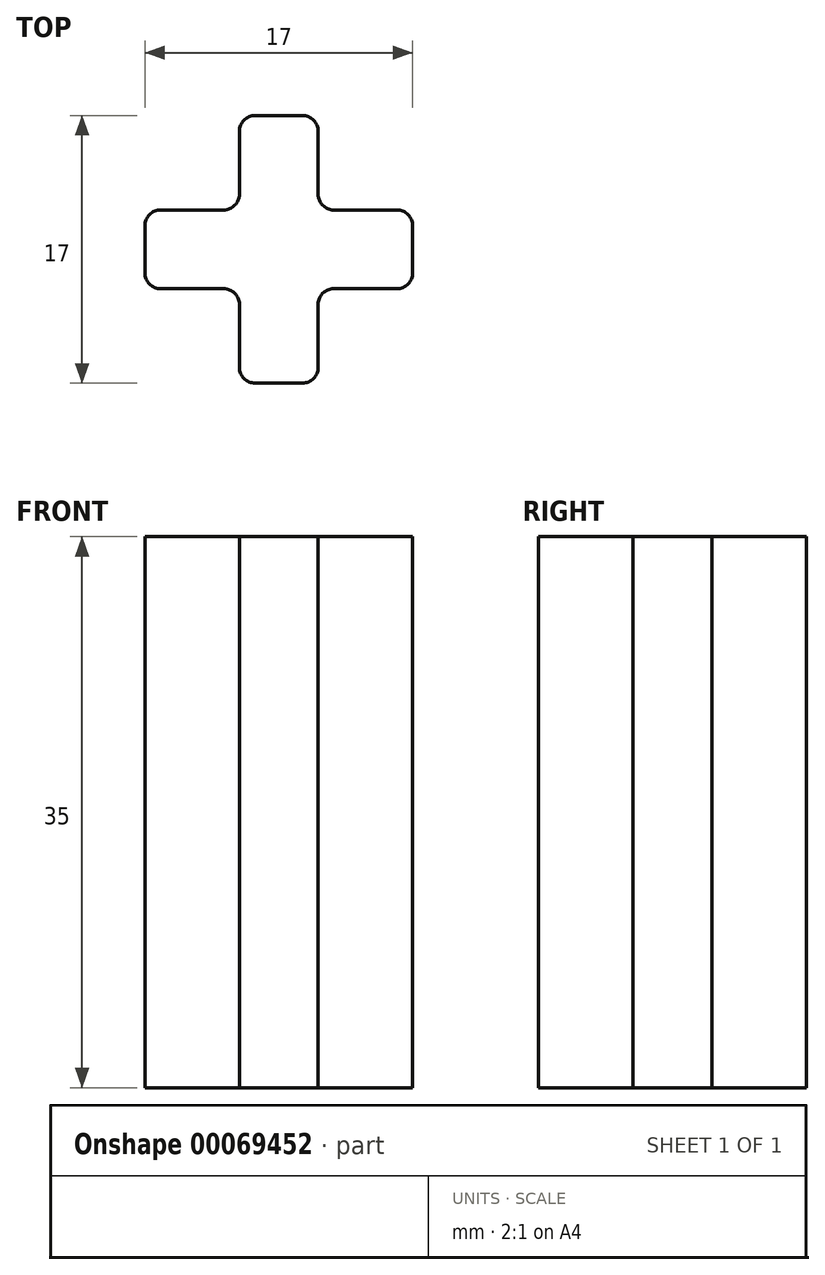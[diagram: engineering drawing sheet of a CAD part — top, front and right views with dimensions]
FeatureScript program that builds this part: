
annotation { "Feature Type Name" : "Feature", "Feature Type Description" : "" }
export const myFeature = defineFeature(function(context is Context, id is Id, definition is map)
    precondition{}
    {
        {
            var Q0;
            Q0=qCreatedBy(makeId("Top.planeOp"),FACE);
            var sketch = newSketch(context, id + "F0", { "sketchPlane" : qUnion([Q0])});
            skLineSegment(sketch, "E0", {"start": v(-2.5, -2.5) * mm, "end": v(-2.5, -8.5) * mm});
            skLineSegment(sketch, "E1", {"start": v(-2.5, -8.5) * mm, "end": v(2.5, -8.5) * mm});
            skLineSegment(sketch, "E2", {"start": v(2.5, -8.5) * mm, "end": v(2.5, -2.5) * mm});
            skLineSegment(sketch, "E3", {"start": v(2.5, -2.5) * mm, "end": v(8.5, -2.5) * mm});
            skLineSegment(sketch, "E4", {"start": v(8.5, -2.5) * mm, "end": v(8.5, 2.5) * mm});
            skLineSegment(sketch, "E5", {"start": v(8.5, 2.5) * mm, "end": v(2.5, 2.5) * mm});
            skLineSegment(sketch, "E6", {"start": v(2.5, 2.5) * mm, "end": v(2.5, 8.5) * mm});
            skLineSegment(sketch, "E7", {"start": v(2.5, 8.5) * mm, "end": v(-2.5, 8.5) * mm});
            skLineSegment(sketch, "E8", {"start": v(-2.5, 8.5) * mm, "end": v(-2.5, 2.5) * mm});
            skLineSegment(sketch, "E9", {"start": v(-2.5, 2.5) * mm, "end": v(-8.5, 2.5) * mm});
            skLineSegment(sketch, "E10", {"start": v(-8.5, 2.5) * mm, "end": v(-8.5, -2.5) * mm});
            skLineSegment(sketch, "E11", {"start": v(-8.5, -2.5) * mm, "end": v(-2.5, -2.5) * mm});
            skSolve(sketch);
        }
        {
            var Q0;
            Q0 = qSketchRegion(id + "F0", true);
            extrude(context, id + "F1", {"entities" : qUnion([Q0]), "depth" : 35 * mm});
        }
        {
            var Q0;
            Q0=makeQuery(id+"F1.opExtrude","SWEPT_EDGE",EDGE,{"disambiguationData":[OSD([sQuery(id+"F0.wireOp",EDGE,"E2"),sQuery(id+"F0.wireOp",EDGE,"E3")])]});
            var Q1;
            Q1=makeQuery(id+"F1.opExtrude","SWEPT_EDGE",EDGE,{"disambiguationData":[OSD([sQuery(id+"F0.wireOp",EDGE,"E0"),sQuery(id+"F0.wireOp",EDGE,"E11")])]});
            fillet(context, id + "F2", {"entities" : qUnion([Q0, Q1]), "radius" : 1 * mm, "tangentPropagation" : true, "allowEdgeOverflow" : false});
        }
        {
            var Q0;
            Q0=makeQuery(id+"F1.opExtrude","SWEPT_EDGE",EDGE,{"disambiguationData":[OSD([sQuery(id+"F0.wireOp",EDGE,"E8"),sQuery(id+"F0.wireOp",EDGE,"E9")])]});
            var Q1;
            Q1=makeQuery(id+"F1.opExtrude","SWEPT_EDGE",EDGE,{"disambiguationData":[OSD([sQuery(id+"F0.wireOp",EDGE,"E5"),sQuery(id+"F0.wireOp",EDGE,"E6")])]});
            fillet(context, id + "F3", {"entities" : qUnion([Q0, Q1]), "radius" : 1 * mm, "allowEdgeOverflow" : false});
        }
        {
            var Q0;
            Q0=makeQuery(id+"F1.opExtrude","SWEPT_EDGE",EDGE,{"disambiguationData":[OSD([sQuery(id+"F0.wireOp",EDGE,"E0"),sQuery(id+"F0.wireOp",EDGE,"E1")])]});
            var Q1;
            Q1=makeQuery(id+"F1.opExtrude","SWEPT_EDGE",EDGE,{"disambiguationData":[OSD([sQuery(id+"F0.wireOp",EDGE,"E1"),sQuery(id+"F0.wireOp",EDGE,"E2")])]});
            var Q2;
            Q2=makeQuery(id+"F1.opExtrude","SWEPT_EDGE",EDGE,{"disambiguationData":[OSD([sQuery(id+"F0.wireOp",EDGE,"E10"),sQuery(id+"F0.wireOp",EDGE,"E11")])]});
            var Q3;
            Q3=makeQuery(id+"F1.opExtrude","SWEPT_EDGE",EDGE,{"disambiguationData":[OSD([sQuery(id+"F0.wireOp",EDGE,"E9"),sQuery(id+"F0.wireOp",EDGE,"E10")])]});
            var Q4;
            Q4=makeQuery(id+"F1.opExtrude","SWEPT_EDGE",EDGE,{"disambiguationData":[OSD([sQuery(id+"F0.wireOp",EDGE,"E7"),sQuery(id+"F0.wireOp",EDGE,"E8")])]});
            var Q5;
            Q5=makeQuery(id+"F1.opExtrude","SWEPT_EDGE",EDGE,{"disambiguationData":[OSD([sQuery(id+"F0.wireOp",EDGE,"E6"),sQuery(id+"F0.wireOp",EDGE,"E7")])]});
            var Q6;
            Q6=makeQuery(id+"F1.opExtrude","SWEPT_EDGE",EDGE,{"disambiguationData":[OSD([sQuery(id+"F0.wireOp",EDGE,"E4"),sQuery(id+"F0.wireOp",EDGE,"E5")])]});
            var Q7;
            Q7=makeQuery(id+"F1.opExtrude","SWEPT_EDGE",EDGE,{"disambiguationData":[OSD([sQuery(id+"F0.wireOp",EDGE,"E3"),sQuery(id+"F0.wireOp",EDGE,"E4")])]});
            fillet(context, id + "F4", {"entities" : qUnion([Q0, Q1, Q2, Q3, Q4, Q5, Q6, Q7]), "radius" : 1 * mm, "tangentPropagation" : true, "allowEdgeOverflow" : false});
        }
    });
